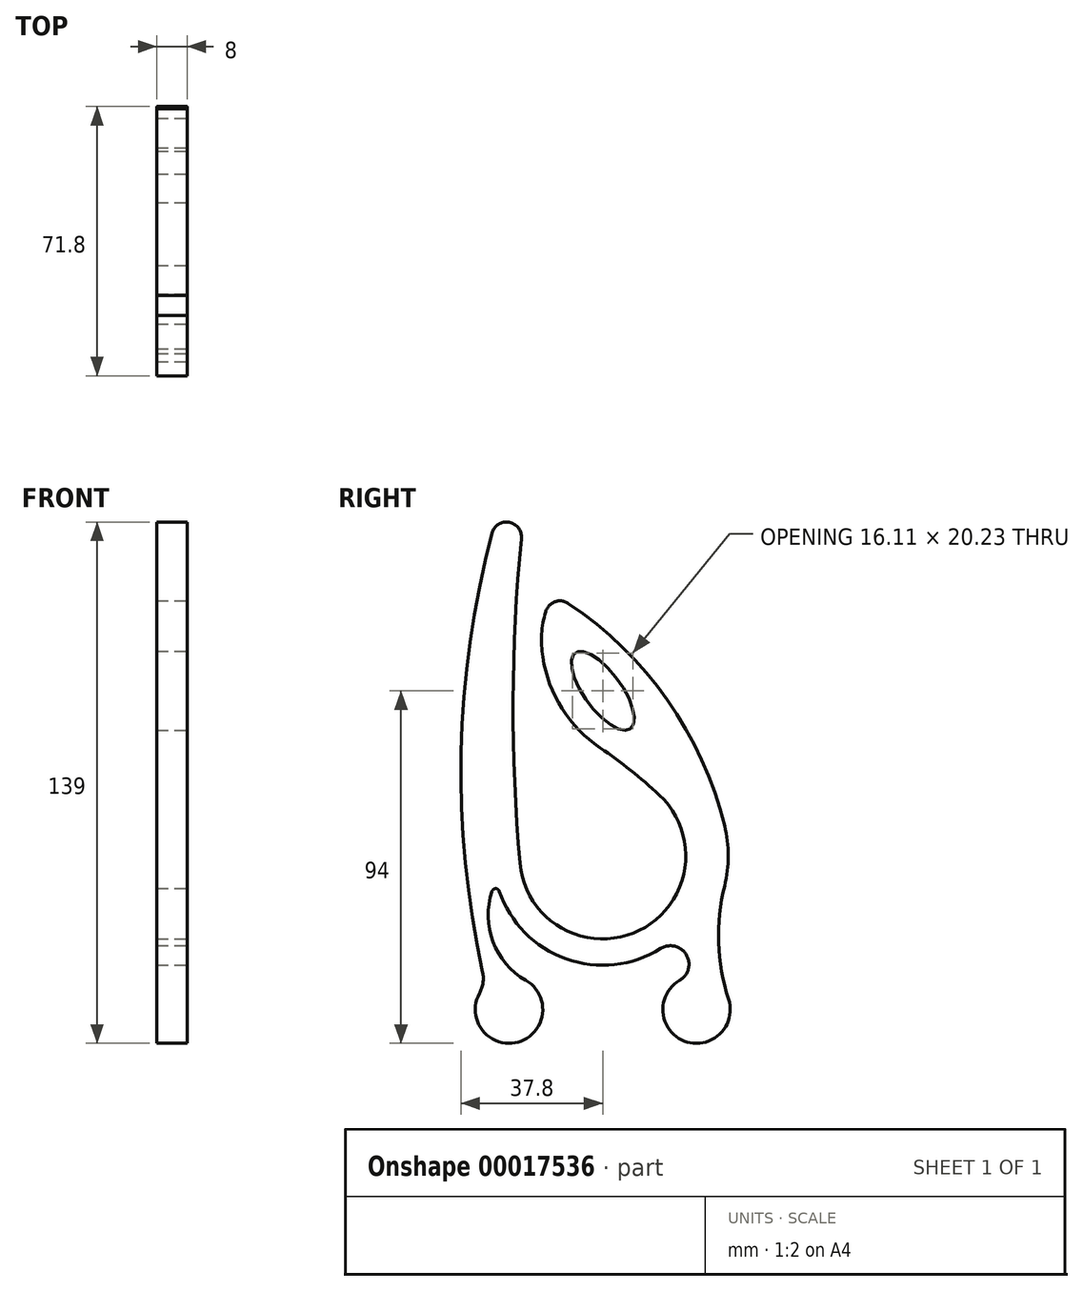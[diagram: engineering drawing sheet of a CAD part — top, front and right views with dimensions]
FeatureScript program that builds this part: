
annotation { "Feature Type Name" : "Feature", "Feature Type Description" : "" }
export const myFeature = defineFeature(function(context is Context, id is Id, definition is map)
    precondition{}
    {
        {
            var Q0;
            Q0=qCreatedBy(makeId("Right.planeOp"), FACE);
            var sketch = newSketch(context, id + "F0", { "sketchPlane" : qUnion([Q0])});
            skCircle(sketch, "E0", {"center": v(0, 0) * mm, "radius": 21.95 * mm, "construction": true});
            skSolve(sketch);
        }
        {
            var Q0;
            Q0=qCreatedBy(makeId("Right.planeOp"), FACE);
            var sketch = newSketch(context, id + "F1", { "sketchPlane" : qUnion([Q0])});
            skLineSegment(sketch, "E1.bottom", {"start": v(-50.5, -34) * mm, "end": v(-33.5, -34) * mm});
            skLineSegment(sketch, "E1.top", {"start": v(-50.5, -67) * mm, "end": v(-33.5, -67) * mm});
            skLineSegment(sketch, "E1.left", {"start": v(-50.5, -34) * mm, "end": v(-50.5, -67) * mm});
            skLineSegment(sketch, "E1.right", {"start": v(-33.5, -34) * mm, "end": v(-33.5, -67) * mm});
            skLineSegment(sketch, "E2.bottom", {"start": v(-33.5, -50) * mm, "end": v(33.5, -50) * mm});
            skLineSegment(sketch, "E2.top", {"start": v(-33.5, -67) * mm, "end": v(33.5, -67) * mm});
            skLineSegment(sketch, "E2.left", {"start": v(-33.5, -50) * mm, "end": v(-33.5, -67) * mm});
            skLineSegment(sketch, "E2.right", {"start": v(33.5, -50) * mm, "end": v(33.5, -67) * mm});
            skLineSegment(sketch, "E3.bottom", {"start": v(33.5, -12) * mm, "end": v(50.5, -12) * mm});
            skLineSegment(sketch, "E3.top", {"start": v(33.5, -67) * mm, "end": v(50.5, -67) * mm});
            skLineSegment(sketch, "E3.left", {"start": v(33.5, -12) * mm, "end": v(33.5, -67) * mm});
            skLineSegment(sketch, "E3.right", {"start": v(50.5, -12) * mm, "end": v(50.5, -67) * mm});
            skLineSegment(sketch, "E4", {"start": v(0, -50) * mm, "end": v(0, 0) * mm, "construction": true});
            skSolve(sketch);
        }
        {
            var Q0;
            Q0=qCreatedBy(makeId("Right.planeOp"), FACE);
            var sketch = newSketch(context, id + "F2", { "sketchPlane" : qUnion([Q0])});
            skArc(sketch, "E5", {"start": v(-22.06, -2) * mm, "mid": v(9.75, -19.89) * mm, "end": v(15.1, 16.21) * mm});
            skArc(sketch, "E6", {"start": v(-32.87, -36.63) * mm, "mid": v(-22.6, -49.67) * mm, "end": v(-20.52, -33.2) * mm});
            skArc(sketch, "E7", {"start": v(20.52, -33.2) * mm, "mid": v(21.76, -49.4) * mm, "end": v(33.57, -38.24) * mm});
            skArc(sketch, "E8", {"start": v(-29.48, -9.4) * mm, "mid": v(-29.27, -22.9) * mm, "end": v(-20.52, -33.2) * mm});
            skArc(sketch, "E9", {"start": v(-32.87, -36.63) * mm, "mid": v(-31.94, -33.9) * mm, "end": v(-32.04, -31.03) * mm});
            skArc(sketch, "E10.MirrorCS", {"start": v(15.44, -24.72) * mm, "mid": v(22.3, -26.38) * mm, "end": v(20.52, -33.2) * mm});
            skArc(sketch, "E11", {"start": v(-27.6, -9.4) * mm, "mid": v(-28.54, -8.73) * mm, "end": v(-29.48, -9.4) * mm});
            skArc(sketch, "E12", {"start": v(-27.6, -9.4) * mm, "mid": v(-9.78, -27.46) * mm, "end": v(15.44, -24.72) * mm});
            skArc(sketch, "E13", {"start": v(-29.55, 86.02) * mm, "mid": v(-37.74, 27.64) * mm, "end": v(-32.04, -31.03) * mm});
            skArc(sketch, "E14", {"start": v(32.5, -8) * mm, "mid": v(30.93, -23.2) * mm, "end": v(33.57, -38.24) * mm});
            skArc(sketch, "E15", {"start": v(32.5, -8) * mm, "mid": v(33.47, 0) * mm, "end": v(32.5, 8) * mm});
            skArc(sketch, "E16", {"start": v(32.5, 8) * mm, "mid": v(17.23, 41.57) * mm, "end": v(-9.17, 67.33) * mm});
            skArc(sketch, "E17", {"start": v(-9.17, 67.33) * mm, "mid": v(-12.76, 67.76) * mm, "end": v(-15.23, 65.11) * mm});
            skArc(sketch, "E18", {"start": v(-15.23, 65.11) * mm, "mid": v(-16.28, 59.1) * mm, "end": v(-16, 53) * mm});
            skLineSegment(sketch, "E19", {"start": v(0, 0) * mm, "end": v(22.15, 0) * mm, "construction": true});
            skArc(sketch, "E20", {"start": v(-16, 53) * mm, "mid": v(-10.85, 39.3) * mm, "end": v(-0.67, 28.78) * mm});
            skArc(sketch, "E21", {"start": v(15.1, 16.21) * mm, "mid": v(7.45, 22.8) * mm, "end": v(-0.67, 28.78) * mm});
            skArc(sketch, "E22", {"start": v(-21.7, 84.6) * mm, "mid": v(-23.93, 41.31) * mm, "end": v(-22.06, -2) * mm});
            skArc(sketch, "E23", {"start": v(-21.7, 84.6) * mm, "mid": v(-24.97, 88.94) * mm, "end": v(-29.55, 86.02) * mm});
            skEllipse(sketch, "E24", {"center": v(0, 44) * mm, "majorRadius": 12.5 * mm, "minorRadius": 5 * mm, "majorAxis": v(0.59, -0.8)});
            skLineSegment(sketch, "E25", {"start": v(-7.35, 54.11) * mm, "end": v(7.35, 33.89) * mm, "construction": true});
            skSolve(sketch);
        }
        {
            var Q0;
            Q0 = qSketchRegion(id + "F2", true);
            extrude(context, id + "F3", {"entities" : qUnion([Q0]), "oppositeDirection" : true, "depth" : 8 * mm, "offsetDistance" : 25 * mm});
        }
    });
